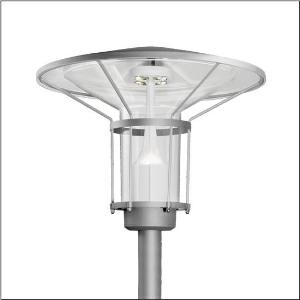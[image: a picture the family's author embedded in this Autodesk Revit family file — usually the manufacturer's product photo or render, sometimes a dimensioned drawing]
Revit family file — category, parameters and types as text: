
# Revit family: laterne_classic_iq___st1_2a_5xa5245af14hp_f3d4
name_source: partatom
category: Lighting Fixtures
units: mm (PartAtom-declared; Revit-internal decimal feet)

## family parameters
Cut with Voids When Loaded = No
Host = Face
Light Source = No
Part Type = Normal
Room Calculation Point = No
Round Connector Dimension = Use Diameter
Shared = No

## types (1)
- --- (1 x LED, 3510 lm, 33.6 W, 2200K)
    Apparent Load = 34 VA
    CIE Flux Codes = 22 60 93 98 100
    Color Rendering = 70
    Color Temperature = 2200K
    Default Elevation = 1800 mm
    Description = Lantern Classic iQ, mast luminaire, Module 540 iQ-SR, primary light control with 3 zone facetted reflector, of plastic, silver coated, highly specular, structured, primary optical cover: cover, of PMMA, transparent, light distribution: ST1.2a, light emission: direct distribution, primary light characteristic: asymmetric, installation type: post-top, LED, High Power LED, rated luminous flux: 3.510lm, luminous efficacy: 105lm/W, light colour: 722, colour temperature: 2200K, control gear: ECG iQ, control: presetting dimming logarithmic, Street-Remote, Auto-Match, Temp-Guard, Lumen-Switch, Night-Set, Smart-Wire, Light-Fading, Desk-Remote (wireless, voltage-free reading and setting of iQ features in the workshop via application-optimized NFC function/RFID function), optimised constant luminous flux control (CLO 2.0), with terminal, 6-pole, max. 2.5mm², mains connection: 230..240V, AC, 50/60Hz, start of lifetime: 34W, end of service life: 36W, reduction: 15W, luminaire housing, upper part, of glass-fibre reinforced polyester, coated, Siteco® metallic grey (DB 702S), diameter: 750mm, height: 596mm, spigot size: d x l = 76 x 70mm (post-top) | with reducer (optional accessory) 60 x 70mm, post-top mast mounting element, of diecast aluminium, coated, Siteco® metallic grey (DB 702S), Module 540 iQ-SR, traffic white (RAL 9016), equipment: Power, protection rating (complete): IP65, insulation class (complete): insulation class II (safety insulation), certification: CE, ENEC, VDE, packaging unit: 1 piece

Light Distribution: ST1.2a
    Height = 596 mm
    Lamp = 1 x LED
    Lamp Light Flux = 3510 lm
    Lamp Power = 33.6 W
    Lamp count = 1
    Length = 750 mm
    Luminous efficacy = 104 lm/W
    Manufacturer = Siteco
    ModVariant = No
    Model = 5XA5245AF14HP
    Number of Poles = 1
    OnlyDefault = Yes
    Power Factor = 1
    Product Name = Laterne Classic iQ | ST1.2a
    Product group = mast luminaire | pylon top
    ProductGroupID = 6100
    Protection Class = Protection class II
    Protection Degree = IP 65
    RLX_Detail_Level = 1
    RLX_Emergency_Light_Flux = 0 lm
    RLX_Emergency_Type = 0
    RLX_Emergency_Type_DB = No
    RlxData = <blob elided: 65013 chars, md5=45e72ac4>
    Socket = socket
    Standby Power = 0 W
    System Light Flux = 3510 lm
    System Power = 34 W
    Type Comments = factory setting: luminous flux: 100 % | dim-lin: 254 | 695 mA
    Type Image = l_1006052.jpg
    URL = http://relux.com
    VarID = @adj_145961
    Voltage = 0 V
    Weight = 0.00 kg
    Width = 0 mm  [stored 0 ft]

note: [stored X ft] marks values corroborated as IEEE doubles in the binary element streams (Revit-internal decimal feet)

## geometry (parser evidence)
native form markers: Blend x4, Sweep x8
no freeform markers — native parametric forms only
